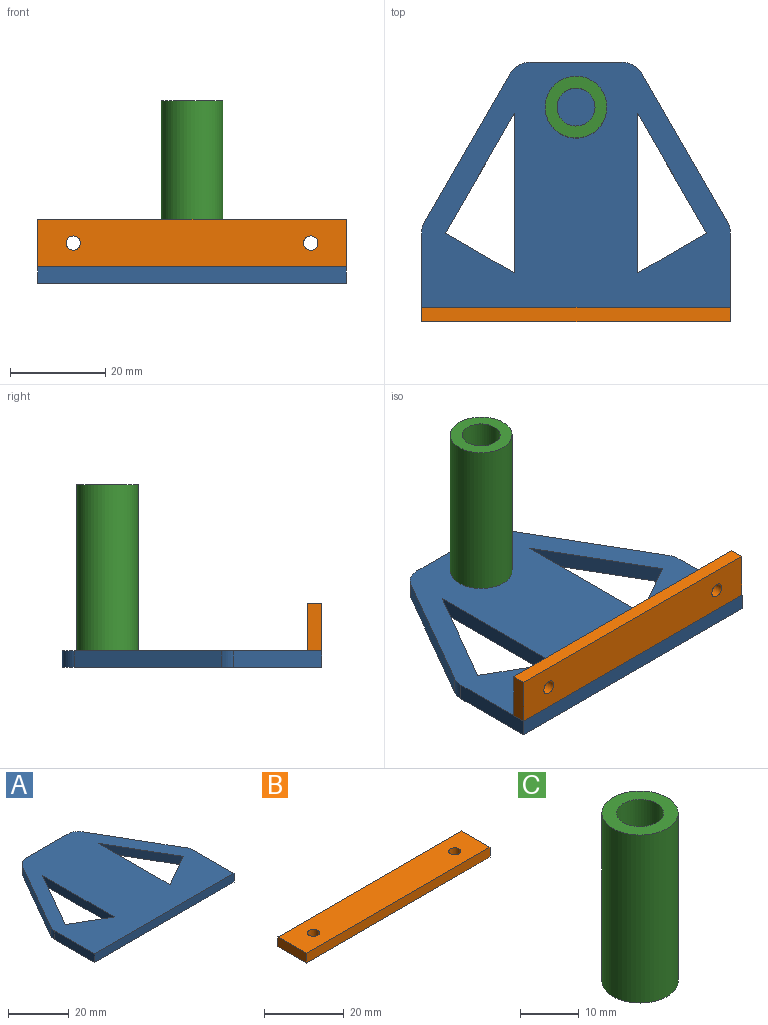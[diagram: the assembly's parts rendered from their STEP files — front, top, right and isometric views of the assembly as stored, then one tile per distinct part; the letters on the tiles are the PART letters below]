
ASSEMBLY  parts=3 mates=2
PART A: 18 faces, bbox 65x54.6x3.5 mm
  f0: cylinder r=5mm len=3.5mm, axis (0,0,-1), area 9.2mm2, adj f1,f15,f16,f17
  f1: plane 30.98x17.89mm, normal (0.87,0.5,0), area 125.2mm2, adj f0,f2,f16,f17
  f2: cylinder r=5mm len=4.33mm, axis (0,0,-1), area 18.3mm2, adj f1,f3,f16,f17
  f3: plane 19.23x3.5mm, normal (0,1,0), area 67.3mm2, adj f2,f4,f16,f17
  f4: cylinder r=5mm len=4.33mm, axis (0,0,-1), area 18.3mm2, adj f3,f5,f16,f17
  f5: plane 30.98x17.89mm, normal (-0.87,0.5,0), area 125.2mm2, adj f4,f6,f16,f17
  f6: cylinder r=5mm len=3.5mm, axis (0,0,-1), area 9.2mm2, adj f5,f7,f16,f17
  f7: plane 18.66x3.5mm, normal (-1,0,0), area 65.3mm2, adj f6,f8,f16,f17
  f8: plane 65x3.5mm, normal (0,-1,0), area 227.5mm2, adj f7,f15,f16,f17
  f9: plane 25.1x14.49mm, normal (-0.87,-0.5,0), area 101.5mm2, adj f10,f13,f16,f17
  f10: plane 14.49x8.37mm, normal (-0.5,0.87,0), area 58.6mm2, adj f9,f13,f16,f17
  f11: plane 14.49x8.37mm, normal (0.5,0.87,0), area 58.6mm2, adj f12,f14,f16,f17
  f12: plane 25.1x14.49mm, normal (0.87,-0.5,0), area 101.5mm2, adj f11,f14,f16,f17
  f13: plane 33.47x3.5mm, normal (1,0,0), area 117.2mm2, adj f9,f10,f16,f17
  f14: plane 33.47x3.5mm, normal (-1,0,0), area 117.2mm2, adj f11,f12,f16,f17
  f15: plane 18.66x3.5mm, normal (1,0,0), area 65.3mm2, adj f0,f8,f16,f17
  f16: plane 65x54.64mm, normal (0,0,1), area 2370.7mm2, adj f0,f1,f2,f3,f4,f5,f6,f7
  f17: plane 65x54.64mm, normal (0,0,-1), area 2370.7mm2, adj f0,f1,f2,f3,f4,f5,f6,f7
PART B: 8 faces, bbox 65x10x3 mm
  f0: plane 65x3mm, normal (0,1,0), area 195mm2, adj f1,f5,f6,f7
  f1: plane 10x3mm, normal (-1,0,0), area 30mm2, adj f0,f2,f6,f7
  f2: plane 65x3mm, normal (0,-1,0), area 195mm2, adj f1,f5,f6,f7
  f3: cylinder r=1.5mm len=3mm, axis (0,0,-1), area 28.3mm2, adj f6,f7
  f4: cylinder r=1.5mm len=3mm, axis (0,0,-1), area 28.3mm2, adj f6,f7
  f5: plane 10x3mm, normal (1,0,0), area 30mm2, adj f0,f2,f6,f7
  f6: plane 65x10mm, normal (0,0,1), area 635.9mm2, adj f0,f1,f2,f3,f4,f5
  f7: plane 65x10mm, normal (0,0,-1), area 635.9mm2, adj f0,f1,f2,f3,f4,f5
PART C: 4 faces, bbox 13x13x35 mm
  f0: cylinder r=4mm len=35mm, axis (0,0,-1), area 879.6mm2, adj f2,f3
  f1: cylinder r=6.5mm len=35mm, axis (0,0,-1), area 1429.4mm2, adj f2,f3
  f2: plane 13x13mm, normal (0,0,1), area 82.5mm2, adj f0,f1
  f3: plane 13x13mm, normal (0,0,-1), area 82.5mm2, adj f0,f1
PLACE A t=(93.1,76.17,-11.12)mm
PLACE B rot(axis=(1,0,0),90deg) t=(-111.46,-63.01,145.74)mm
PLACE C rot(axis=(1,0,0),180deg) t=(42.77,-76.04,27.38)mm
MATE fastened B.f2 <-> A.f16  axis (0,0,-1) through (-56.19,-66.01,-7.62)mm
MATE fastened C.f0 <-> A.f16  axis (0,0,1) through (-56.19,-20.87,-7.62)mm
